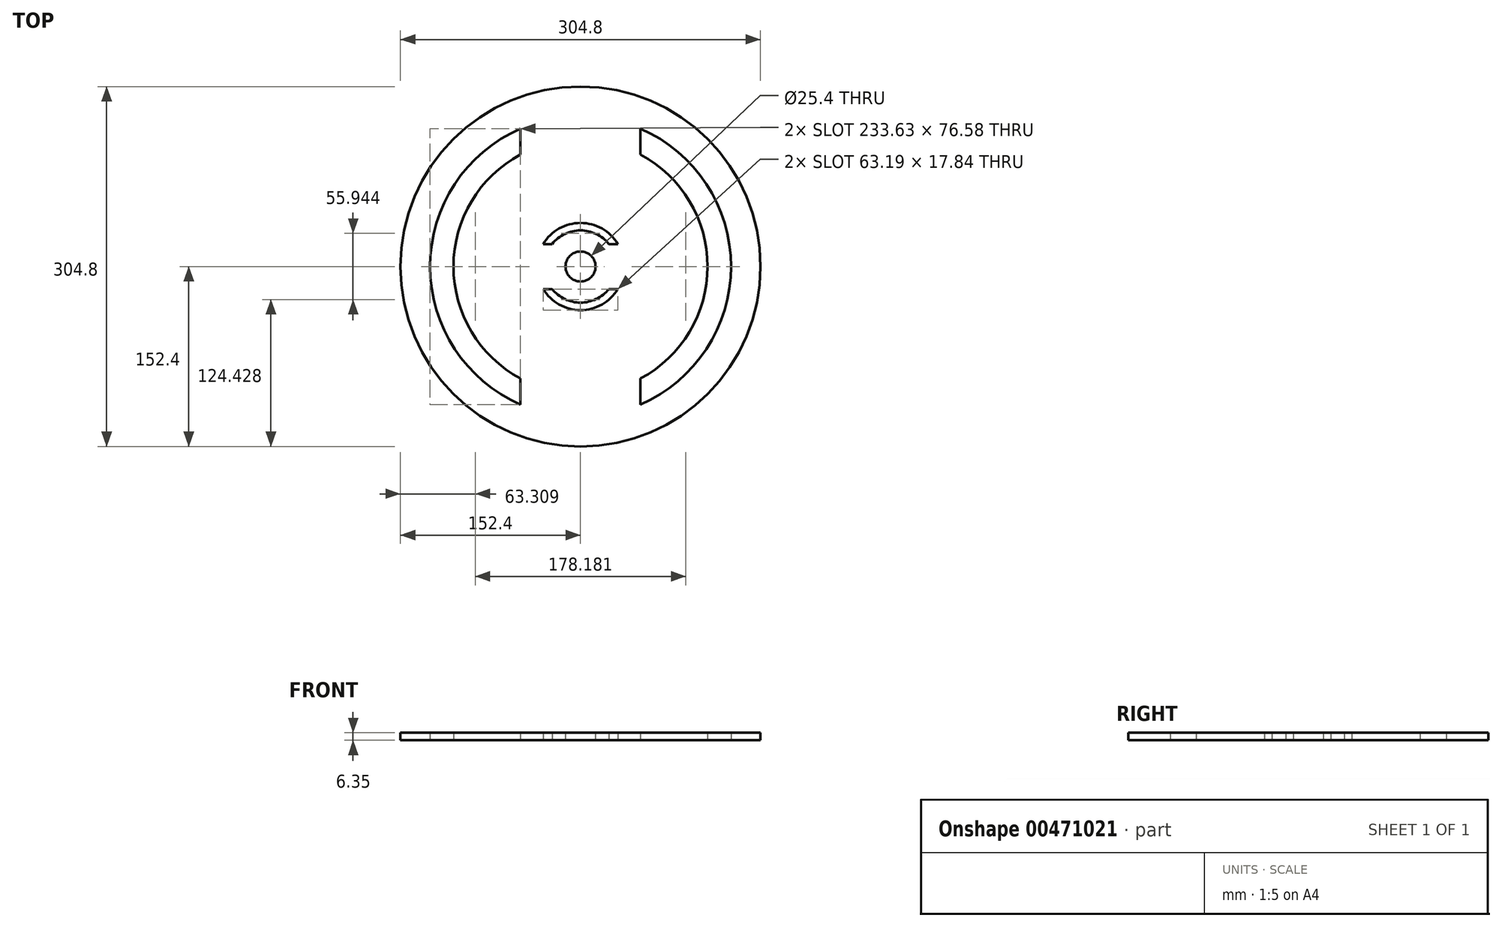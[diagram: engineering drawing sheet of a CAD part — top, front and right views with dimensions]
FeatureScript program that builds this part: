
annotation { "Feature Type Name" : "Feature", "Feature Type Description" : "" }
export const myFeature = defineFeature(function(context is Context, id is Id, definition is map)
    precondition{}
    {
        {
            var Q0;
            Q0=qCreatedBy(makeId("Top.planeOp"),FACE);
            var sketch = newSketch(context, id + "F0", { "sketchPlane" : qUnion([Q0])});
            skArc(sketch, "E0", {"start": v(-50.8, 116.81) * mm, "mid": v(-127.38, 0) * mm, "end": v(-50.8, -116.81) * mm});
            skCircle(sketch, "E1", {"center": v(0, 0) * mm, "radius": 152.4 * mm});
            skArc(sketch, "E2", {"start": v(-50.8, 94.82) * mm, "mid": v(-107.57, 0) * mm, "end": v(-50.8, -94.82) * mm});
            skLineSegment(sketch, "E3", {"start": v(-50.8, 116.81) * mm, "end": v(-50.8, 94.82) * mm});
            skLineSegment(sketch, "E4", {"start": v(0, -152.4) * mm, "end": v(0, 152.4) * mm, "construction": true});
            skLineSegment(sketch, "E5.trimOffspring", {"start": v(-50.8, -94.82) * mm, "end": v(-50.8, -116.81) * mm});
            skLineSegment(sketch, "E6.MirrorCS", {"start": v(50.8, 116.81) * mm, "end": v(50.8, 94.82) * mm});
            skArc(sketch, "E7.MirrorCS", {"start": v(50.8, 116.81) * mm, "mid": v(127.38, 0) * mm, "end": v(50.8, -116.81) * mm});
            skArc(sketch, "E8.MirrorCS", {"start": v(50.8, 94.82) * mm, "mid": v(107.57, 0) * mm, "end": v(50.8, -94.82) * mm});
            skLineSegment(sketch, "E9.MirrorCS", {"start": v(50.8, -94.82) * mm, "end": v(50.8, -116.81) * mm});
            skLineSegment(sketch, "E10", {"start": v(-152.4, 0) * mm, "end": v(152.4, 0) * mm, "construction": true});
            skCircle(sketch, "E11", {"center": v(0, 0) * mm, "radius": 12.7 * mm});
            skArc(sketch, "E12", {"start": v(-31.6, -19.05) * mm, "mid": v(0, -36.9) * mm, "end": v(31.6, -19.05) * mm});
            skArc(sketch, "E13", {"start": v(-23.96, -19.05) * mm, "mid": v(0, -30.6) * mm, "end": v(23.96, -19.05) * mm});
            skLineSegment(sketch, "E14", {"start": v(-31.6, 19.05) * mm, "end": v(-23.96, 19.05) * mm});
            skLineSegment(sketch, "E15.MirrorCS", {"start": v(-31.6, -19.05) * mm, "end": v(-23.96, -19.05) * mm});
            skLineSegment(sketch, "E16.trimOffspring", {"start": v(23.96, 19.05) * mm, "end": v(31.6, 19.05) * mm});
            skArc(sketch, "E17.trimOffspring", {"start": v(23.96, 19.05) * mm, "mid": v(0, 30.6) * mm, "end": v(-23.96, 19.05) * mm});
            skArc(sketch, "E18.trimOffspring", {"start": v(31.6, 19.05) * mm, "mid": v(0, 36.9) * mm, "end": v(-31.6, 19.05) * mm});
            skLineSegment(sketch, "E19.trimOffspring", {"start": v(23.96, -19.05) * mm, "end": v(31.6, -19.05) * mm});
            skSolve(sketch);
        }
        {
            var Q0;
            Q0 = qSketchRegion(id + "F0", true);
            extrude(context, id + "F1", {"entities" : qUnion([Q0]), "depth" : 6.35 * mm, "offsetDistance" : 25.4 * mm});
        }
    });
